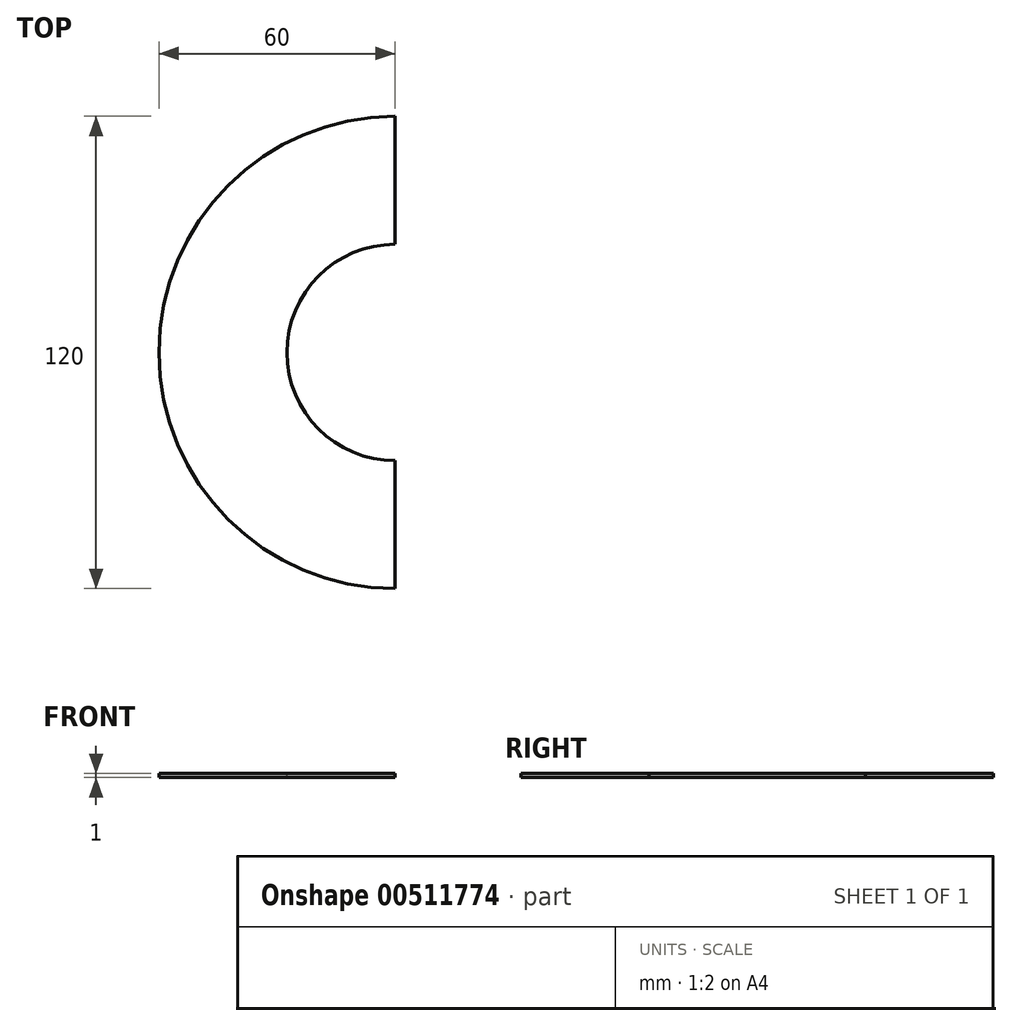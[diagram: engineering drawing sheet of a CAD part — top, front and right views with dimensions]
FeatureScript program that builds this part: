
annotation { "Feature Type Name" : "Feature", "Feature Type Description" : "" }
export const myFeature = defineFeature(function(context is Context, id is Id, definition is map)
    precondition{}
    {
        {
            var Q0;
            Q0=qCreatedBy(makeId("Top.planeOp"),FACE);
            var sketch = newSketch(context, id + "F0", { "sketchPlane" : qUnion([Q0])});
            skArc(sketch, "E0", {"start": v(0, 60) * mm, "mid": v(-60, 0) * mm, "end": v(0, -60) * mm});
            skArc(sketch, "E1", {"start": v(0, 27.5) * mm, "mid": v(-27.5, 0) * mm, "end": v(0, -27.5) * mm});
            skLineSegment(sketch, "E2", {"start": v(0, -60) * mm, "end": v(0, -27.5) * mm});
            skLineSegment(sketch, "E3.trimOffspring", {"start": v(0, 27.5) * mm, "end": v(0, 60) * mm});
            skSolve(sketch);
        }
        {
            var Q0;
            Q0=makeQuery(id+"F0.imprint","IMPRINT",FACE,{"disambiguationData":[TD([[makeQuery(id+"F0.imprint","IMPRINT",EDGE,{"derivedFrom":sQuery(id+"F0.wireOp",EDGE,"E0")}),1.0]])]});
            extrude(context, id + "F1", {"entities" : qUnion([Q0]), "oppositeDirection" : true, "depth" : 1 * mm});
        }
    });
